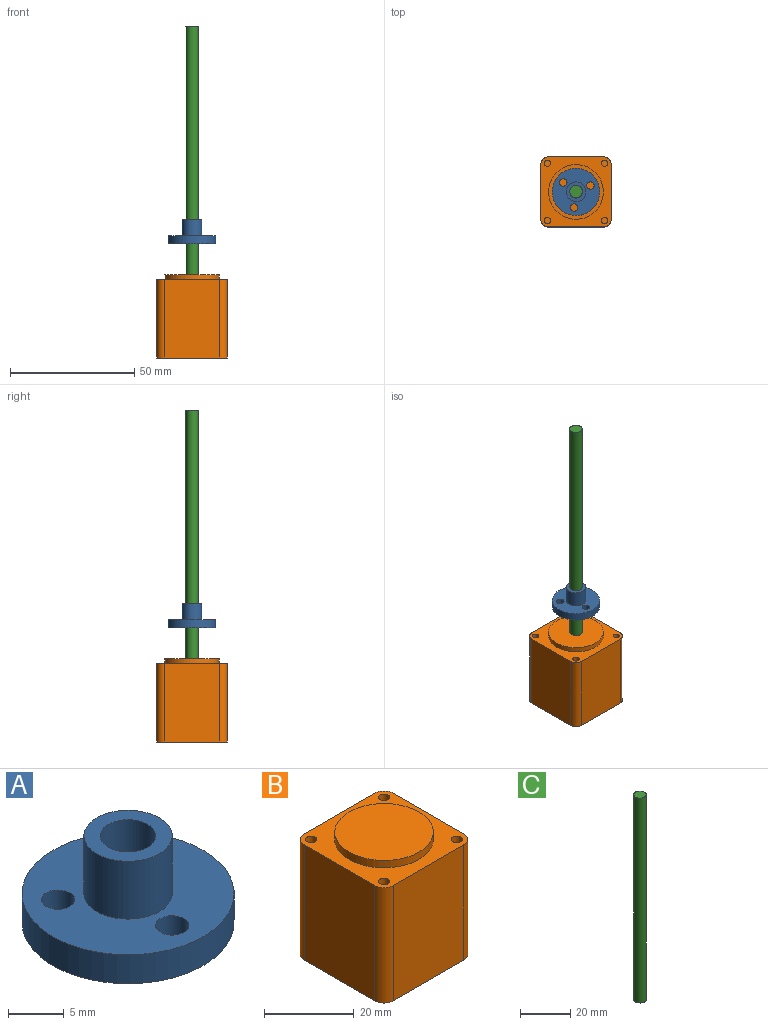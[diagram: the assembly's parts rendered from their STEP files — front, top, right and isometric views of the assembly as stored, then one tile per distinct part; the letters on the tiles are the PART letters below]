
ASSEMBLY  parts=3 mates=2
PART A: 9 faces, bbox 19.1x19.1x9.5 mm
  f0: cylinder r=2.5mm len=9.53mm, axis (0,0,-1), area 149.7mm2, adj f3,f5
  f1: cylinder r=9.53mm len=19.05mm, axis (0,0,-1), area 190.3mm2, adj f2,f3
  f2: plane 19.05x19.05mm, normal (0,0,1), area 214.3mm2, adj f1,f4,f6,f7,f8
  f3: plane 19.05x19.05mm, normal (0,0,-1), area 244.2mm2, adj f0,f1,f6,f7,f8
  f4: cylinder r=3.97mm len=7.94mm, axis (0,0,-1), area 158.4mm2, adj f2,f5
  f5: plane 7.94x7.94mm, normal (0,0,1), area 29.9mm2, adj f0,f4
  f6: cylinder r=1.5mm len=3.18mm, axis (0,0,-1), area 30mm2, adj f2,f3
  f7: cylinder r=1.5mm len=3.18mm, axis (0,0,-1), area 30mm2, adj f2,f3
  f8: cylinder r=1.5mm len=3.18mm, axis (0,0,-1), area 30mm2, adj f2,f3
PART B: 20 faces, bbox 28.2x28.2x33.5 mm
  f0: plane 28.2x28.2mm, normal (0,0,1), area 387.7mm2, adj f1,f3,f4,f5,f6,f8,f10,f12
  f1: plane 31.5x22.2mm, normal (-1,0,0), area 699.3mm2, adj f0,f2,f17,f19
  f2: plane 28.2x28.2mm, normal (0,0,-1), area 787.5mm2, adj f1,f3,f4,f5,f16,f17,f18,f19
  f3: plane 31.5x22.2mm, normal (1,0,0), area 699.3mm2, adj f0,f2,f16,f18
  f4: plane 31.5x22.2mm, normal (0,-1,0), area 699.3mm2, adj f0,f2,f18,f19
  f5: plane 31.5x22.2mm, normal (0,1,0), area 699.3mm2, adj f0,f2,f16,f17
  f6: cylinder r=1.25mm len=3.5mm, axis (0,0,1), area 27.5mm2, adj f0,f7
  f7: plane 2.5x2.5mm, normal (0,0,1), area 4.9mm2, adj f6
  f8: cylinder r=1.25mm len=3.5mm, axis (0,0,1), area 27.5mm2, adj f0,f9
  f9: plane 2.5x2.5mm, normal (0,0,1), area 4.9mm2, adj f8
  f10: cylinder r=1.25mm len=3.5mm, axis (0,0,1), area 27.5mm2, adj f0,f11
  f11: plane 2.5x2.5mm, normal (0,0,1), area 4.9mm2, adj f10
  f12: cylinder r=1.25mm len=3.5mm, axis (0,0,1), area 27.5mm2, adj f0,f13
  f13: plane 2.5x2.5mm, normal (0,0,1), area 4.9mm2, adj f12
  f14: cylinder r=11mm len=22mm, axis (0,0,-1), area 138.2mm2, adj f0,f15
  f15: plane 22x22mm, normal (0,0,1), area 380.1mm2, adj f14
  f16: cylinder r=3mm len=31.5mm, axis (0,0,1), area 148.4mm2, adj f0,f2,f3,f5
  f17: cylinder r=3mm len=31.5mm, axis (0,0,-1), area 148.4mm2, adj f0,f1,f2,f5
  f18: cylinder r=3mm len=31.5mm, axis (0,0,-1), area 148.4mm2, adj f0,f2,f3,f4
  f19: cylinder r=3mm len=31.5mm, axis (0,0,1), area 148.4mm2, adj f0,f1,f2,f4
PART C: 3 faces, bbox 5x5x100 mm
  f0: cylinder r=2.5mm len=100mm, axis (0,0,-1), area 1570.8mm2, adj f1,f2
  f1: plane 5x5mm, normal (0,0,1), area 19.6mm2, adj f0
  f2: plane 5x5mm, normal (0,0,-1), area 19.6mm2, adj f0
PLACE A t=(-22.01,27.76,36.45)mm
PLACE B t=(-22.01,27.76,23.95)mm fixed
PLACE C t=(-22.01,27.76,25.95)mm
MATE slider A.f0 <-> C.f0  axis (0,0,-1) through (-22.01,27.76,38.45)mm
MATE fastened C.f0 <-> B.f14  axis (0,0,-1) through (-22.01,27.76,25.95)mm
